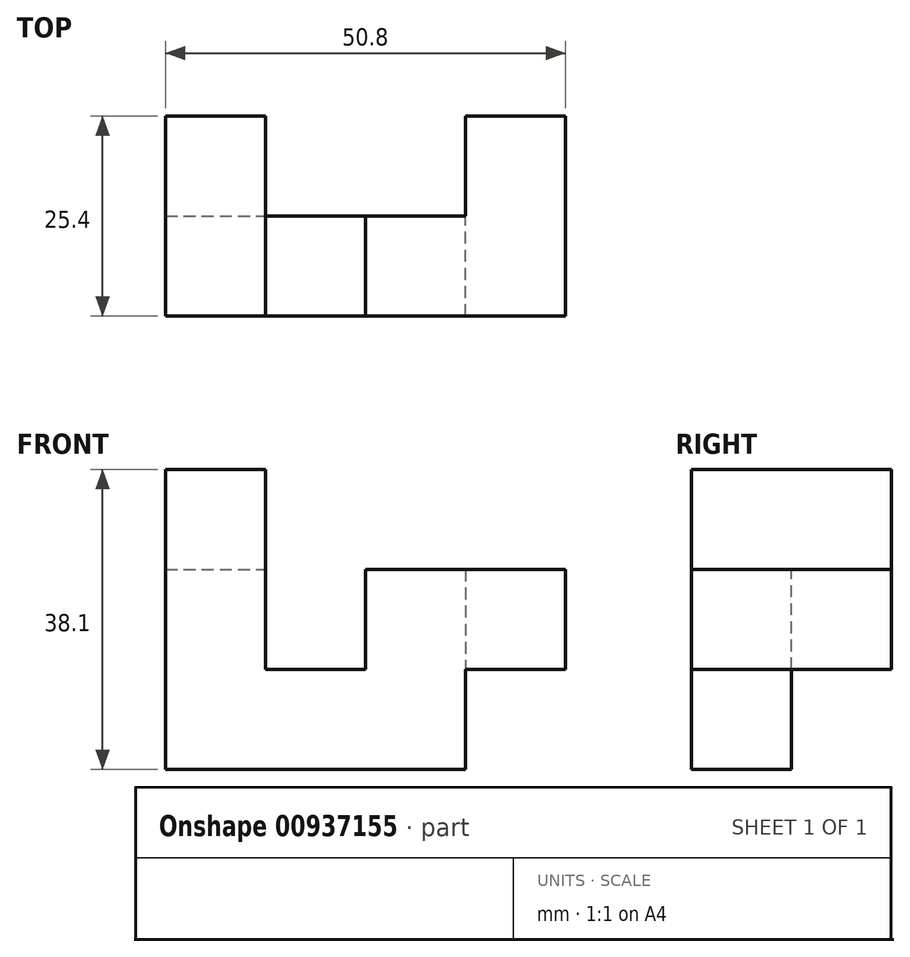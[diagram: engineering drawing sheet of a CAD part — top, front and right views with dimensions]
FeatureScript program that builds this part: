
annotation { "Feature Type Name" : "Feature", "Feature Type Description" : "" }
export const myFeature = defineFeature(function(context is Context, id is Id, definition is map)
    precondition{}
    {
        {
            var Q0;
            Q0=qCreatedBy(makeId("Front.planeOp"),FACE);
            var sketch = newSketch(context, id + "F0", { "sketchPlane" : qUnion([Q0])});
            skLineSegment(sketch, "E0.bottom", {"start": v(-61.09, 62.84) * mm, "end": v(-48.39, 62.84) * mm});
            skLineSegment(sketch, "E0.top", {"start": v(-61.09, 50.14) * mm, "end": v(-48.39, 50.14) * mm});
            skLineSegment(sketch, "E0.left", {"start": v(-61.09, 62.84) * mm, "end": v(-61.09, 50.14) * mm});
            skLineSegment(sketch, "E0.right", {"start": v(-48.39, 62.84) * mm, "end": v(-48.39, 50.14) * mm});
            skLineSegment(sketch, "E1.top", {"start": v(-61.09, 37.44) * mm, "end": v(-48.39, 37.44) * mm});
            skLineSegment(sketch, "E1.left", {"start": v(-61.09, 50.14) * mm, "end": v(-61.09, 37.44) * mm});
            skLineSegment(sketch, "E1.right", {"start": v(-48.39, 50.14) * mm, "end": v(-48.39, 37.44) * mm});
            skLineSegment(sketch, "E2.top", {"start": v(-61.09, 24.74) * mm, "end": v(-48.39, 24.74) * mm});
            skLineSegment(sketch, "E2.left", {"start": v(-61.09, 37.44) * mm, "end": v(-61.09, 24.74) * mm});
            skLineSegment(sketch, "E2.right", {"start": v(-48.39, 37.44) * mm, "end": v(-48.39, 24.74) * mm});
            skLineSegment(sketch, "E3.bottom", {"start": v(-48.39, 24.74) * mm, "end": v(-35.69, 24.74) * mm});
            skLineSegment(sketch, "E3.top", {"start": v(-48.39, 37.44) * mm, "end": v(-35.69, 37.44) * mm});
            skLineSegment(sketch, "E3.left", {"start": v(-48.39, 24.74) * mm, "end": v(-48.39, 37.44) * mm});
            skLineSegment(sketch, "E3.right", {"start": v(-35.69, 24.74) * mm, "end": v(-35.69, 37.44) * mm});
            skLineSegment(sketch, "E4.bottom", {"start": v(-35.69, 37.44) * mm, "end": v(-22.99, 37.44) * mm});
            skLineSegment(sketch, "E4.top", {"start": v(-35.69, 24.74) * mm, "end": v(-22.99, 24.74) * mm});
            skLineSegment(sketch, "E4.left", {"start": v(-35.69, 37.44) * mm, "end": v(-35.69, 24.74) * mm});
            skLineSegment(sketch, "E4.right", {"start": v(-22.99, 37.44) * mm, "end": v(-22.99, 24.74) * mm});
            skLineSegment(sketch, "E5.top", {"start": v(-35.69, 50.14) * mm, "end": v(-22.99, 50.14) * mm});
            skLineSegment(sketch, "E5.left", {"start": v(-35.69, 37.44) * mm, "end": v(-35.69, 50.14) * mm});
            skLineSegment(sketch, "E5.right", {"start": v(-22.99, 37.44) * mm, "end": v(-22.99, 50.14) * mm});
            skLineSegment(sketch, "E6.bottom", {"start": v(-22.99, 50.14) * mm, "end": v(-10.29, 50.14) * mm});
            skLineSegment(sketch, "E6.top", {"start": v(-22.99, 37.44) * mm, "end": v(-10.29, 37.44) * mm});
            skLineSegment(sketch, "E6.left", {"start": v(-22.99, 50.14) * mm, "end": v(-22.99, 37.44) * mm});
            skLineSegment(sketch, "E6.right", {"start": v(-10.29, 50.14) * mm, "end": v(-10.29, 37.44) * mm});
            skSolve(sketch);
        }
        {
            var Q0;
            Q0=makeQuery(id+"F0.imprint","IMPRINT",FACE,{"disambiguationData":[TD([[makeQuery(id+"F0.imprint","IMPRINT",EDGE,{"derivedFrom":sQuery(id+"F0.wireOp",EDGE,"E0.top")}),-1.0]])]});
            var Q1;
            Q1=makeQuery(id+"F0.imprint","IMPRINT",FACE,{"disambiguationData":[TD([[makeQuery(id+"F0.imprint","IMPRINT",EDGE,{"derivedFrom":sQuery(id+"F0.wireOp",EDGE,"E1.top")}),-1.0]])]});
            var Q2;
            Q2=makeQuery(id+"F0.imprint","IMPRINT",FACE,{"disambiguationData":[TD([[makeQuery(id+"F0.imprint","IMPRINT",EDGE,{"derivedFrom":sQuery(id+"F0.wireOp",EDGE,"E4.top")}),1.0]])]});
            var Q3;
            Q3=makeQuery(id+"F0.imprint","IMPRINT",FACE,{"disambiguationData":[TD([[makeQuery(id+"F0.imprint","IMPRINT",EDGE,{"derivedFrom":sQuery(id+"F0.wireOp",EDGE,"E3.bottom")}),1.0]])]});
            var Q4;
            Q4=makeQuery(id+"F0.imprint","IMPRINT",FACE,{"disambiguationData":[TD([[makeQuery(id+"F0.imprint","IMPRINT",EDGE,{"derivedFrom":sQuery(id+"F0.wireOp",EDGE,"E4.bottom")}),1.0]])]});
            extrude(context, id + "F1", {"entities" : qUnion([Q0, Q1, Q2, Q3, Q4]), "depth" : 12.7 * mm, "offsetDistance" : 25.4 * mm});
        }
        {
            var Q0;
            Q0=makeQuery(id+"F0.imprint","IMPRINT",FACE,{"disambiguationData":[TD([[makeQuery(id+"F0.imprint","IMPRINT",EDGE,{"derivedFrom":sQuery(id+"F0.wireOp",EDGE,"E0.bottom")}),-1.0]])]});
            var Q1;
            Q1=makeQuery(id+"F0.imprint","IMPRINT",FACE,{"disambiguationData":[TD([[makeQuery(id+"F0.imprint","IMPRINT",EDGE,{"derivedFrom":sQuery(id+"F0.wireOp",EDGE,"E6.bottom")}),-1.0]])]});
            extrude(context, id + "F2", {"entities" : qUnion([Q0, Q1]), "operationType" : NewBodyOperationType.ADD, "endBound" : BoundingType.SYMMETRIC, "depth" : 25.4 * mm, "offsetDistance" : 25.4 * mm});
        }
    });
